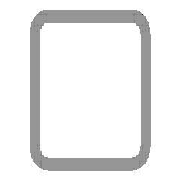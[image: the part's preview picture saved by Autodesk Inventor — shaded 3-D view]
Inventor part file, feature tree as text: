
AUTODESK INVENTOR PART (.ipt)
format: ipt  version: 2025.1 (Build 291241020, 241B)  size: 134,656 bytes
history: native  units: mm (DEFAULTED — no unit token found)
features: other x4, sketch x1, plane x1
ambient origin geometry x8: Origin, YZ Plane, XZ Plane, XY Plane, X Axis, Y Axis, Z Axis, Center Point
bodies: Solid1 (feature_tree), Body (feature_tree)
feature tree (6):
  parser-record x1  (decoder bookkeeping rows leaked as tree rows — omitted from the tree; the rows remain in map.json)
  other  "Driven Length"
  other  "Start Plane"
  other  "End Plane"
  sketch  "Sketch3"  dims[d3=550.0mm d4=0.0mm d7=8.0mm d9=100.0mm d11=100.0mm d12=4.0mm d13=100.0mm d14=650.0mm d15=50.0mm d16=50.0mm d17=90.0deg d18=550.0mm]
  plane  "Work Plane3"
